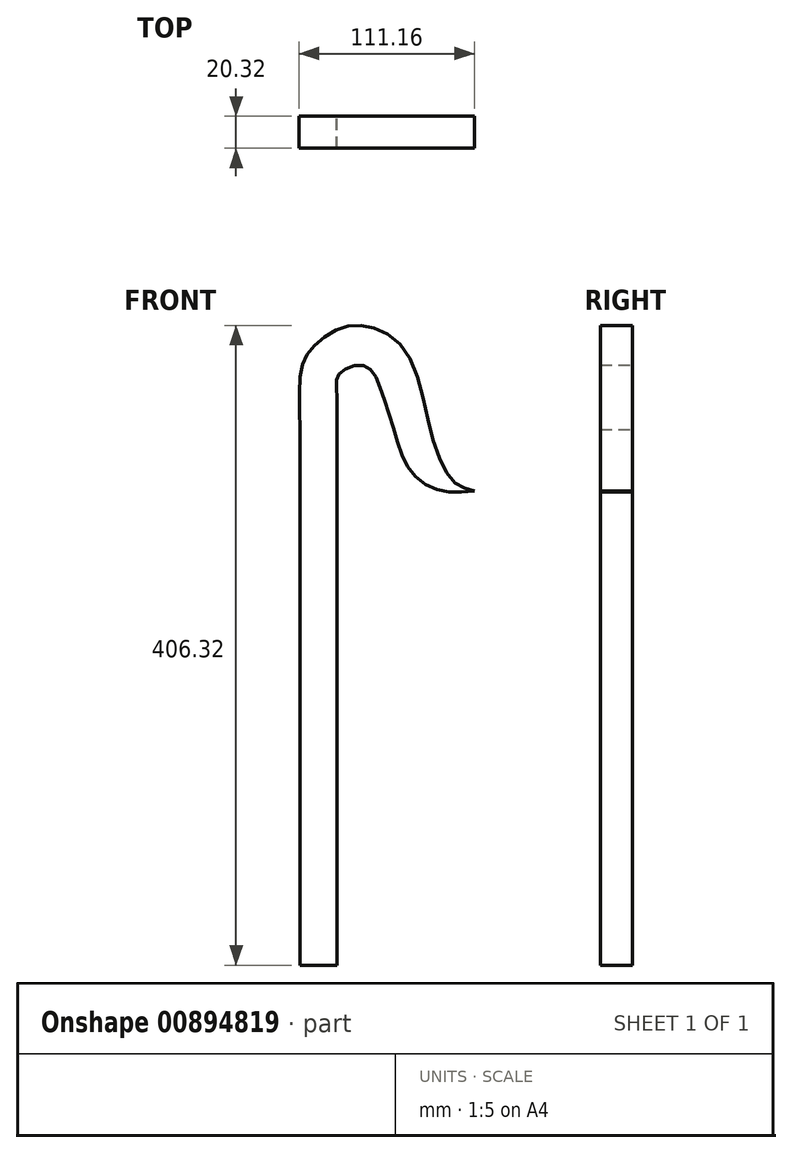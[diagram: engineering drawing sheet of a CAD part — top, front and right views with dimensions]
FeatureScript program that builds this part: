
annotation { "Feature Type Name" : "Feature", "Feature Type Description" : "" }
export const myFeature = defineFeature(function(context is Context, id is Id, definition is map)
    precondition{}
    {
        {
            var Q0;
            Q0=qCreatedBy(makeId("Front.planeOp"),FACE);
            var sketch = newSketch(context, id + "F0", { "sketchPlane" : qUnion([Q0])});
            skFitSpline(sketch, "E0", {"points": [v(97.64, 312.3) * mm, v(85.09, 317.57) * mm, v(70.5, 348.35) * mm, v(54.7, 400.2) * mm, v(30.81, 416.4) * mm, v(10.56, 414.77) * mm, v(-6.05, 402.22) * mm, v(-12.53, 387.64) * mm, v(-12.93, 351.18) * mm], "startDerivative": vector(-146.39, 31.52) * mm, "endDerivative": vector(11.6, -279.65) * mm});
            skFitSpline(sketch, "E1", {"points": [v(10.56, 351.18) * mm, v(10.15, 379.13) * mm, v(10.96, 385.2) * mm, v(19.47, 391.28) * mm, v(30.4, 390.47) * mm, v(37.3, 379.13) * mm, v(46.6, 351.18) * mm, v(56.33, 326.07) * mm, v(74.96, 312.7) * mm, v(97.64, 312.3) * mm], "startDerivative": vector(-1.94, 239.14) * mm, "endDerivative": vector(185.15, 19.41) * mm});
            skLineSegment(sketch, "E2", {"start": v(10.56, 351.18) * mm, "end": v(10.47, 10.97) * mm});
            skLineSegment(sketch, "E3", {"start": v(10.47, 10.97) * mm, "end": v(10.56, 351.18) * mm});
            skLineSegment(sketch, "E4", {"start": v(-12.93, 351.18) * mm, "end": v(-12.93, 10.97) * mm});
            skLineSegment(sketch, "E5", {"start": v(-12.93, 10.97) * mm, "end": v(10.47, 10.97) * mm});
            skSolve(sketch);
        }
        {
            var Q0;
            Q0=makeQuery(id+"F0.imprint","IMPRINT",FACE,{"disambiguationData":[TD([[makeQuery(id+"F0.imprint","IMPRINT",EDGE,{"derivedFrom":sQuery(id+"F0.wireOp",EDGE,"E0")}),1.0]])]});
            extrude(context, id + "F1", {"entities" : qUnion([Q0]), "depth" : 10.16 * mm, "offsetDistance" : 25.4 * mm});
        }
        {
            var Q0;
            Q0=makeQuery(id+"F1.opExtrude","CAP_FACE",FACE,{"disambiguationData":[OSD([sQuery(id+"F0.wireOp",EDGE,"E0"),sQuery(id+"F0.wireOp",EDGE,"E1"),sQuery(id+"F0.wireOp",EDGE,"E3"),sQuery(id+"F0.wireOp",EDGE,"E4"),sQuery(id+"F0.wireOp",EDGE,"E5")])],"isStart":true});
            extrude(context, id + "F2", {"entities" : qUnion([Q0]), "operationType" : NewBodyOperationType.ADD, "depth" : 10.16 * mm, "offsetDistance" : 25.4 * mm});
        }
    });
